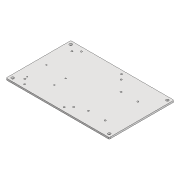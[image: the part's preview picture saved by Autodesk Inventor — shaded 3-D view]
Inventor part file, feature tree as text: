
AUTODESK INVENTOR PART (.ipt)
format: ipt  version: 2020 (Build 240168000, 168)  size: 158,720 bytes
history: native  units: mm
features: other x37, extrude x5, sketch x5, fillet x1
ambient origin geometry x8: Origin, YZ Plane, XZ Plane, XY Plane, X Axis, Y Axis, Z Axis, Center Point
bodies: Body1 (feature_tree)
feature tree (48):
  other  "Sólido1"
  extrude  "Extrusão1"  Depth=158.0mm
  fillet  "Arredondamento1"  Radius=4.0mm
  extrude  "Extrusão2"  Depth=2.0mm
  extrude  "Extrusão3"  Depth=6.7mm
  extrude  "Extrusão4"  Depth=8.0mm
  extrude  "Extrusão5"  Depth=10.0mm
  sketch  "Esboço1"  dims[d0=252.0mm d1=158.0mm d2=4.0mm d3=0.0mm]
  sketch  "Esboço2"  dims[d4=2.0mm d5=6.7mm]
  sketch  "Esboço3"  dims[d6=6.7mm d7=6.7mm]
  other  "Referência1"
  other  "Referência2"
  other  "Referência3"
  other  "Referência4"
  other  "Referência5"
  other  "Referência6"
  other  "Referência7"
  other  "Referência8"
  other  "Referência9"
  other  "Referência10"
  other  "Referência11"
  other  "Referência12"
  other  "Referência13"
  other  "Referência14"
  sketch  "Esboço4"  dims[d8=6.7mm d9=8.0mm]
  other  "Referência15"
  other  "Referência16"
  other  "Referência17"
  other  "Referência18"
  other  "Referência19"
  other  "Referência20"
  other  "Referência21"
  other  "Referência22"
  sketch  "Esboço5"  dims[d10=8.0mm d11=8.0mm d12=8.0mm d13=8.0mm d14=8.0mm d15=8.0mm d16=8.0mm d17=10.0mm d18=0.0mm d19=10.0mm d20=0.0mm d21=10.0mm d22=0.0mm d23=10.0mm d24=0.0mm]
  other  "Referência23"
  other  "Referência24"
  other  "Referência25"
  other  "Referência26"
  other  "<userpath>\OneDrive\Área de Trabalho\Calorimetro 2022\Inventor\Calorímetro.iam"
  other  "Calorímetro.iam"
  other  "ATX Power Supply v1:1"
  other  "Cover:1"
  other  "suporte-fonte:1"
  other  "suporte_fechamento:2"
  other  "suporte_fechamento2:3"
  other  "suporte_fechamento:1"
  other  "suporte_fechamento2:2"
  other  "Mega:1"
